# Revit family: Loft ladder LWT
name_source: partatom
category: Modele ogólne
revit_build: Autodesk Revit 2015 (Build: 20140223_1515(x64)
units: mm (PartAtom-declared; Revit-internal decimal feet)

## types (5) — shared parameters
Bimobject Category = Construction - Stairs
CSI MasterFormat 2016 Code = 06430
CSI MasterFormat 2016 Title = Stairs, Spiral, Guardrails
CSI UniFormat II Code = C2010
CSI UniFormat II Title = Stair Construction
Handrail Material = Fakro - Handrail
Hatch Material = Fakro - Hatch
IFC Classification = Stair
Kod zespołu = C2010140
Ladder Material = Fakro - ladder
Material Secondary = Fakro - steel
Model = LWT
NBS Reference = 45-30-75/405
NBS Reference Description = Timber loft ladders
Opis = Loft ladder
Producent = FAKRO
Stile Ends Material = Fakro - Stile Ends
UNSPC Category = Ladders and scaffolding
UNSPC Code = 301915
URL = www.fakro.com
Uniclass 1.4 Code = L43212
Uniclass 1.4 Description = Loft ladders
Uniclass 2.0 Code = 25-30-85-36
Uniclass 2.0 Description = Hardwood loft ladders
Uniclass 2015 Code = PR_25_30_85
Uniclass 2015 Title = Stair and ladder units
box = pinewood
box height = 220 mm  [stored 0.721785 ft]
distance between treads = 250 mm  [stored 0.82021 ft]
hatch board retraction after opening = 65 mm  [stored 0.213255 ft]
hatch colour = white
hatch thickness = 80 mm  [stored 0.262467 ft]
heat transfer coefficient U [W/m2K] = 0.51
height of folded ladder = 330 mm  [stored 1.08268 ft]
ladder = pinewood
lock = yes
maximum loading = 160.00 kg
number of sections = 3
seal = 3
thermal insulation thickness = 74 mm  [stored 0.242782 ft]
tread length in the ladder = 34
tread thickness = 20 mm  [stored 0.0656168 ft]
tread width in the ladder = 80 mm  [stored 0.262467 ft]
treads = anti-slip. equal to ladder stringers
zero-valued in all types: Domyślna rzędna

## per-type parameters (varying)
| type | Obj Type | box internal dimensions | distance after ladder unfolding | max room height | swing space |
| LWT - 60x120 | 4 mm  [stored 0.0131234 ft] | 54x114 | 1270 mm | 2800 mm  [stored 9.18635 ft] | 1600 mm  [stored 5.24934 ft] |
| LWT - 70x120 | 10 mm  [stored 0.0328084 ft] | 64x114 | 1270 mm | 2800 mm  [stored 9.18635 ft] | 1600 mm  [stored 5.24934 ft] |
| LWT - 70x130 | 11 mm  [stored 0.0360892 ft] | 64x124 | 1350 mm  [stored 4.42913 ft] | 3050 mm  [stored 10.0066 ft] | 1750 mm  [stored 5.74147 ft] |
| LWT - 70x140 | 12 mm  [stored 0.0393701 ft] | 64x134 | 1350 mm  [stored 4.42913 ft] | 3050 mm  [stored 10.0066 ft] | 1750 mm  [stored 5.74147 ft] |
| LWT - 60x130 | 5 mm  [stored 0.0164042 ft] | 54x124 | 1350 mm  [stored 4.42913 ft] | 3050 mm  [stored 10.0066 ft] | 1750 mm  [stored 5.74147 ft] |

note: [stored X ft] marks values corroborated as IEEE doubles in the binary element streams (Revit-internal decimal feet)
